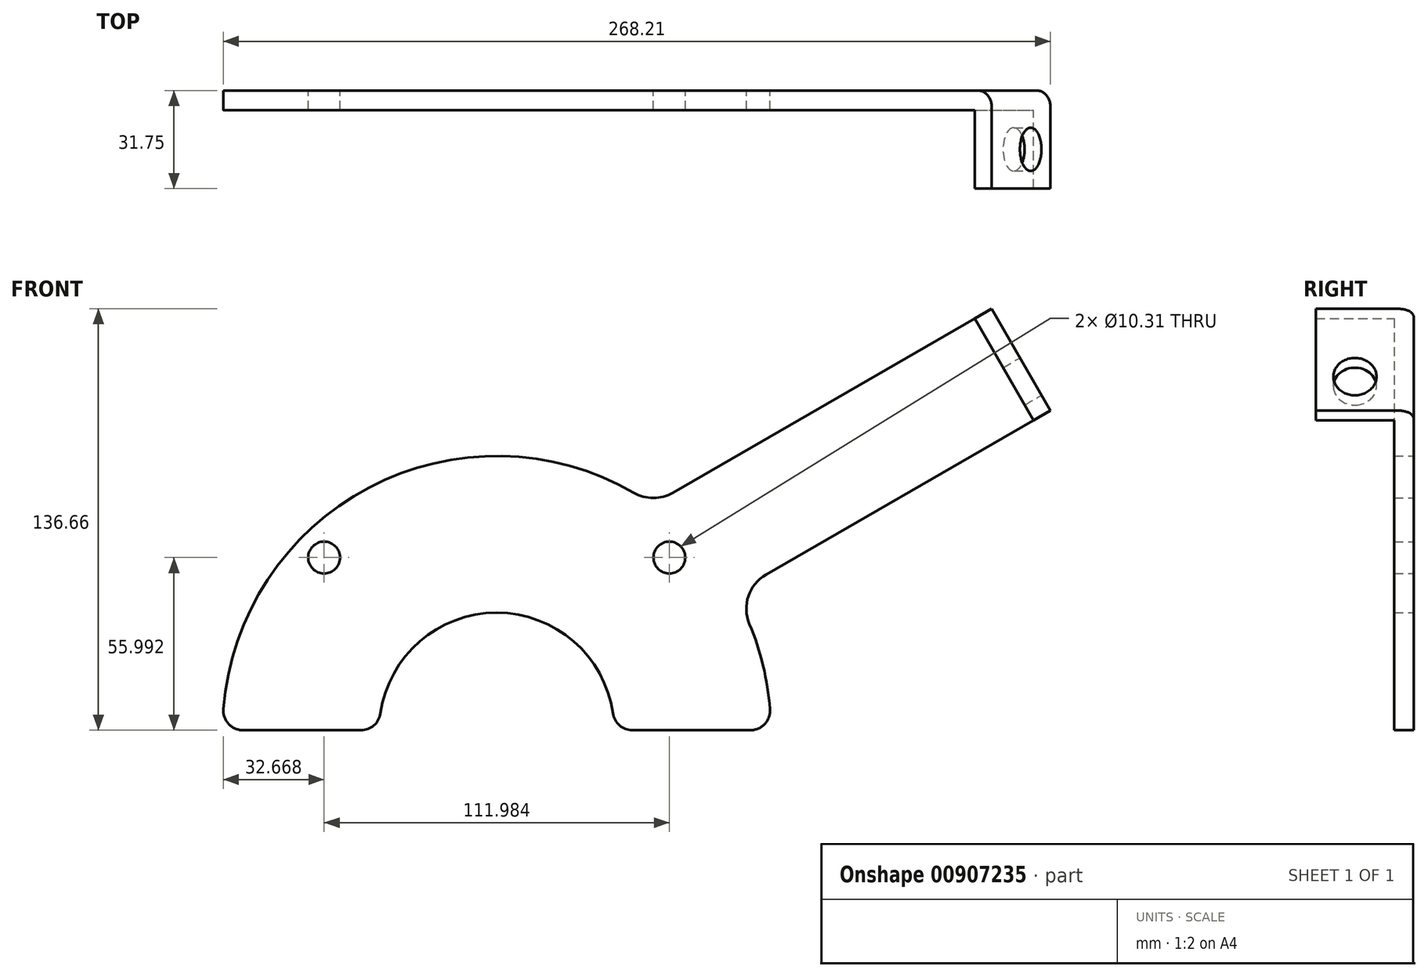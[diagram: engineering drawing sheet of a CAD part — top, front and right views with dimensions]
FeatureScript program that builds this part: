
annotation { "Feature Type Name" : "Feature", "Feature Type Description" : "" }
export const myFeature = defineFeature(function(context is Context, id is Id, definition is map)
    precondition{}
    {
        {
            var Q0;
            Q0=qCreatedBy(makeId("Front.planeOp"),FACE);
            var sketch = newSketch(context, id + "F0", { "sketchPlane" : qUnion([Q0])});
            skArc(sketch, "E0", {"start": v(88.9, 0) * mm, "mid": v(85.87, 23) * mm, "end": v(76.99, 44.45) * mm});
            skArc(sketch, "E1", {"start": v(38.1, 0) * mm, "mid": v(0, 38.1) * mm, "end": v(-38.1, 0) * mm});
            skLineSegment(sketch, "E2", {"start": v(-88.9, 0) * mm, "end": v(-38.1, 0) * mm});
            skLineSegment(sketch, "E3.trimOffspring", {"start": v(38.1, 0) * mm, "end": v(88.9, 0) * mm});
            skLineSegment(sketch, "E4", {"start": v(0, 0) * mm, "end": v(76.99, 44.45) * mm, "construction": true});
            skLineSegment(sketch, "E5", {"start": v(76.99, 44.45) * mm, "end": v(179.55, 103.66) * mm});
            skLineSegment(sketch, "E6", {"start": v(179.55, 103.66) * mm, "end": v(160.5, 136.66) * mm});
            skLineSegment(sketch, "E7", {"start": v(160.5, 136.66) * mm, "end": v(50.51, 73.16) * mm});
            skArc(sketch, "E8.trimOffspring", {"start": v(50.51, 73.16) * mm, "mid": v(-41.3, 78.72) * mm, "end": v(-88.9, 0) * mm});
            skSolve(sketch);
        }
        {
            var Q0;
            Q0=qSketchRegion(id+"F0",true);
            extrude(context, id + "F1", {"entities" : qUnion([Q0]), "depth" : 6.35 * mm, "offsetDistance" : 25.4 * mm});
        }
        {
            var Q0;
            Q0=makeQuery(id+"F1.opExtrude","CAP_FACE",FACE,{"disambiguationData":[OSD([sQuery(id+"F0.wireOp",EDGE,"E0"),sQuery(id+"F0.wireOp",EDGE,"E1")])],"isStart":false});
            var sketch = newSketch(context, id + "F2", { "sketchPlane" : qUnion([Q0])});
            skLineSegment(sketch, "E9", {"start": v(0, 0) * mm, "end": v(-62.86, 62.86) * mm, "construction": true});
            skPoint(sketch, "E10.center", {"position": v(0, 0) * mm});
            skLineSegment(sketch, "E11", {"start": v(0, 0) * mm, "end": v(62.86, 62.86) * mm, "construction": true});
            skPoint(sketch, "E12", {"position": v(-62.86, 62.86) * mm});
            skPoint(sketch, "E13", {"position": v(62.86, 62.86) * mm});
            skCircle(sketch, "E14", {"center": v(-56, 56) * mm, "radius": 7 * mm});
            skCircle(sketch, "E15", {"center": v(56, 56) * mm, "radius": 7 * mm});
            skSolve(sketch);
        }
        {
            var Q0;
            Q0=sQuery(id+"F2.wireOp",VERTEX,"E14.center");
            var Q1;
            Q1=sQuery(id+"F2.wireOp",VERTEX,"E15.center");
            var Q2;
            Q2=sQuery(id+"F2.wireOp",VERTEX,"63c57d3f-0896-44f0-a177-1cb718a14314");
            var Q3;
            Q3=sQuery(id+"F2.wireOp",VERTEX,"531b54bc-60c9-4a52-ae1a-907c0e3ef8af");
            var Q4;
            Q4=makeQuery(id+"F1.opExtrude","SWEPT_BODY",BODY,{"disambiguationData":[OSD([sQuery(id+"F0.wireOp",EDGE,"E0"),sQuery(id+"F0.wireOp",EDGE,"E1")])]});
            hole(context, id + "F3", {"style" : HoleStyle.SIMPLE, "endStyle" : HoleEndStyle.THROUGH, "standardTappedOrClearance" : lookupTablePath({ "fit" : "Normal (ASME)", "standard" : "ANSI", "size" : "3/8", "type" : "Clearance" }), "standardBlindInLast" : lookupTablePath({ "fit" : "Normal", "standard" : "ANSI", "engagement" : "75%", "pitch" : "16 tpi", "size" : "3/8", "type" : "Clearance & tapped" }), "holeDiameter" : 10.3 * mm, "majorDiameter" : 9.52 * mm, "isTappedThrough" : true, "tappedDepth" : 8.47 * mm, "tapClearance" : 3, "locations" : qUnion([Q0, Q1, Q2, Q3]), "scope" : qUnion([Q4]), "startStyle" : HoleStartStyle.SKETCH});
        }
        {
            var Q0;
            Q0=makeQuery(id+"F1.opExtrude","CAP_FACE",FACE,{"disambiguationData":[OSD([sQuery(id+"F0.wireOp",EDGE,"E0"),sQuery(id+"F0.wireOp",EDGE,"E1"),sQuery(id+"F0.wireOp",EDGE,"E2"),sQuery(id+"F0.wireOp",EDGE,"E3.trimOffspring"),sQuery(id+"F0.wireOp",EDGE,"E5"),sQuery(id+"F0.wireOp",EDGE,"E6"),sQuery(id+"F0.wireOp",EDGE,"E7"),sQuery(id+"F0.wireOp",EDGE,"E8.trimOffspring")])],"isStart":false});
            var sketch = newSketch(context, id + "F4", { "sketchPlane" : qUnion([Q0])});
            skLineSegment(sketch, "E16", {"start": v(155, 133.48) * mm, "end": v(174.05, 100.49) * mm});
            skLineSegment(sketch, "E17", {"start": v(174.05, 100.49) * mm, "end": v(179.55, 103.66) * mm});
            skLineSegment(sketch, "E18", {"start": v(179.55, 103.66) * mm, "end": v(160.5, 136.66) * mm});
            skLineSegment(sketch, "E19", {"start": v(160.5, 136.66) * mm, "end": v(155, 133.48) * mm});
            skSolve(sketch);
        }
        {
            var Q0;
            Q0=makeQuery(id+"F4.imprint","IMPRINT",FACE,{"disambiguationData":[TD([[makeQuery(id+"F4.imprint","IMPRINT",EDGE,{"derivedFrom":sQuery(id+"F4.wireOp",EDGE,"E16")}),1.0]])]});
            extrude(context, id + "F5", {"entities" : qUnion([Q0]), "operationType" : NewBodyOperationType.ADD, "depth" : 25.4 * mm, "offsetDistance" : 25.4 * mm});
        }
        {
            var Q0;
            Q0=makeQuery(id+"F5.opExtrude","SWEPT_FACE",FACE,{"disambiguationData":[OSD([sQuery(id+"F4.wireOp",EDGE,"E16")])]});
            var sketch = newSketch(context, id + "F6", { "sketchPlane" : qUnion([Q0])});
            skPoint(sketch, "E20", {"position": v(19.05, 12.7) * mm});
            skPoint(sketch, "E20.positionSnap0", {"position": v(19.05, 38.1) * mm});
            skSolve(sketch);
        }
        {
            var Q0;
            Q0=sQuery(id+"F6.wireOp",VERTEX,"E20");
            var Q1;
            Q1=makeQuery(id+"F1.opExtrude","SWEPT_BODY",BODY,{"disambiguationData":[OSD([sQuery(id+"F0.wireOp",EDGE,"E0"),sQuery(id+"F0.wireOp",EDGE,"E1"),sQuery(id+"F0.wireOp",EDGE,"E2"),sQuery(id+"F0.wireOp",EDGE,"E3.trimOffspring"),sQuery(id+"F0.wireOp",EDGE,"E5"),sQuery(id+"F0.wireOp",EDGE,"E6"),sQuery(id+"F0.wireOp",EDGE,"E7"),sQuery(id+"F0.wireOp",EDGE,"E8.trimOffspring")])]});
            hole(context, id + "F7", {"style" : HoleStyle.SIMPLE, "endStyle" : HoleEndStyle.THROUGH, "standardTappedOrClearance" : lookupTablePath({ "standard" : "ISO", "size" : "14", "type" : "Drilled" }), "standardBlindInLast" : lookupTablePath({ "standard" : "ISO", "size" : "14", "type" : "Drilled" }), "holeDiameter" : 14 * mm, "majorDiameter" : 6.35 * mm, "isTappedThrough" : true, "tappedDepth" : 8.47 * mm, "tapClearance" : 3, "locations" : qUnion([Q0]), "scope" : qUnion([Q1]), "startStyle" : HoleStartStyle.SKETCH});
        }
        {
            var Q0;
            Q0=makeQuery(id+"F1.opExtrude","SWEPT_EDGE",EDGE,{"disambiguationData":[OSD([sQuery(id+"F0.wireOp",EDGE,"E7"),sQuery(id+"F0.wireOp",EDGE,"E8.trimOffspring")])]});
            var Q1;
            Q1=makeQuery(id+"F1.opExtrude","SWEPT_EDGE",EDGE,{"disambiguationData":[OSD([sQuery(id+"F0.wireOp",EDGE,"E0"),sQuery(id+"F0.wireOp",EDGE,"E5")])]});
            fillet(context, id + "F8", {"entities" : qUnion([Q0, Q1]), "radius" : 12.7 * mm, "tangentPropagation" : true, "allowEdgeOverflow" : false});
        }
        {
            var Q0;
            Q0=makeQuery(id+"F1.opExtrude","CAP_EDGE",EDGE,{"disambiguationData":[OSD([sQuery(id+"F0.wireOp",EDGE,"E6")])],"isStart":true});
            fillet(context, id + "F9", {"entities" : qUnion([Q0]), "radius" : 5.08 * mm, "tangentPropagation" : true, "allowEdgeOverflow" : false});
        }
        {
            var Q0;
            Q0=makeQuery(id+"F1.opExtrude","SWEPT_EDGE",EDGE,{"disambiguationData":[OSD([sQuery(id+"F0.wireOp",EDGE,"E0"),sQuery(id+"F0.wireOp",EDGE,"E3.trimOffspring")])]});
            var Q1;
            Q1=makeQuery(id+"F1.opExtrude","SWEPT_EDGE",EDGE,{"disambiguationData":[OSD([sQuery(id+"F0.wireOp",EDGE,"E1"),sQuery(id+"F0.wireOp",EDGE,"E3.trimOffspring")])]});
            var Q2;
            Q2=makeQuery(id+"F1.opExtrude","SWEPT_EDGE",EDGE,{"disambiguationData":[OSD([sQuery(id+"F0.wireOp",EDGE,"E1"),sQuery(id+"F0.wireOp",EDGE,"E2")])]});
            var Q3;
            Q3=makeQuery(id+"F1.opExtrude","SWEPT_EDGE",EDGE,{"disambiguationData":[OSD([sQuery(id+"F0.wireOp",EDGE,"E2"),sQuery(id+"F0.wireOp",EDGE,"E8.trimOffspring")])]});
            fillet(context, id + "F10", {"entities" : qUnion([Q0, Q1, Q2, Q3]), "radius" : 6.35 * mm, "tangentPropagation" : true, "allowEdgeOverflow" : false});
        }
    });
